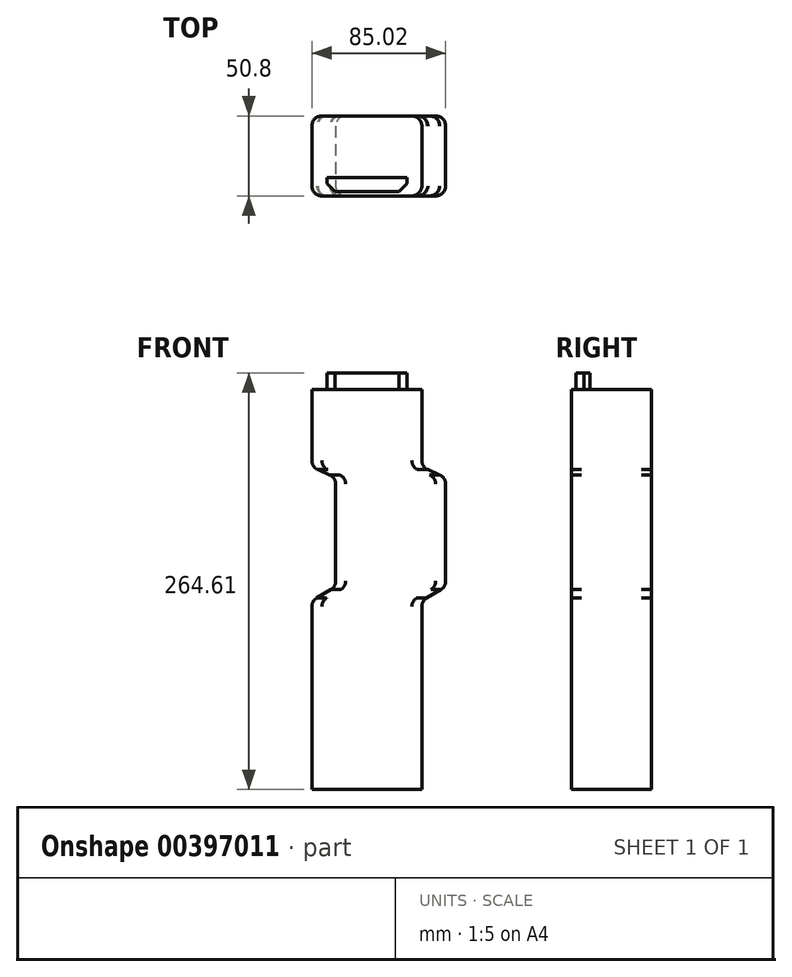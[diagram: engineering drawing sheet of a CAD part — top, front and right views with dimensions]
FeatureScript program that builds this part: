
annotation { "Feature Type Name" : "Feature", "Feature Type Description" : "" }
export const myFeature = defineFeature(function(context is Context, id is Id, definition is map)
    precondition{}
    {
        {
            var Q0;
            Q0=qCreatedBy(makeId("Top.planeOp"),FACE);
            var sketch = newSketch(context, id + "F0", { "sketchPlane" : qUnion([Q0])});
            skLineSegment(sketch, "E0.bottom", {"start": v(-28.57, 25.4) * mm, "end": v(28.57, 25.4) * mm});
            skLineSegment(sketch, "E0.top", {"start": v(-28.57, -25.4) * mm, "end": v(28.58, -25.4) * mm});
            skLineSegment(sketch, "E0.left", {"start": v(-34.92, 19.05) * mm, "end": v(-34.92, -19.05) * mm});
            skLineSegment(sketch, "E0.right", {"start": v(34.93, 19.05) * mm, "end": v(34.93, -19.05) * mm});
            skLineSegment(sketch, "E1", {"start": v(0, 25.4) * mm, "end": v(0, -25.4) * mm, "construction": true});
            skLineSegment(sketch, "E2", {"start": v(-34.92, 0) * mm, "end": v(34.93, 0) * mm, "construction": true});
            skPoint(sketch, "E2.endSnap0", {"position": v(34.93, 0) * mm});
            skPoint(sketch, "E3.visualSharp", {"position": v(-34.92, 25.4) * mm});
            skArc(sketch, "E3.filletArc", {"start": v(-28.57, 25.4) * mm, "mid": v(-33.07, 23.54) * mm, "end": v(-34.93, 19.05) * mm});
            skPoint(sketch, "E4.visualSharp", {"position": v(-34.92, -25.4) * mm});
            skArc(sketch, "E4.filletArc", {"start": v(-34.93, -19.05) * mm, "mid": v(-33.07, -23.54) * mm, "end": v(-28.57, -25.4) * mm});
            skPoint(sketch, "E5.visualSharp", {"position": v(34.93, -25.4) * mm});
            skArc(sketch, "E5.filletArc", {"start": v(28.58, -25.4) * mm, "mid": v(33.07, -23.54) * mm, "end": v(34.93, -19.05) * mm});
            skPoint(sketch, "E6.visualSharp", {"position": v(34.93, 25.4) * mm});
            skArc(sketch, "E6.filletArc", {"start": v(34.93, 19.05) * mm, "mid": v(33.07, 23.54) * mm, "end": v(28.57, 25.4) * mm});
            skSolve(sketch);
        }
        {
            var Q0;
            Q0=qCreatedBy(makeId("Front.planeOp"),FACE);
            var sketch = newSketch(context, id + "F1", { "sketchPlane" : qUnion([Q0])});
            skLineSegment(sketch, "E7", {"start": v(0, 0) * mm, "end": v(0, 116.26) * mm});
            skLineSegment(sketch, "E8", {"start": v(3.12, 121.72) * mm, "end": v(12.04, 127) * mm});
            skLineSegment(sketch, "E9", {"start": v(15.16, 132.47) * mm, "end": v(15.16, 194.1) * mm});
            skLineSegment(sketch, "E10", {"start": v(11.34, 199.93) * mm, "end": v(3.82, 203.2) * mm});
            skLineSegment(sketch, "E11", {"start": v(0, 209.02) * mm, "end": v(0, 254) * mm});
            skPoint(sketch, "E12.visualSharp", {"position": v(0, 204.86) * mm});
            skArc(sketch, "E12.filletArc", {"start": v(0, 209.02) * mm, "mid": v(1.04, 205.54) * mm, "end": v(3.82, 203.2) * mm});
            skPoint(sketch, "E13.visualSharp", {"position": v(15.16, 198.27) * mm});
            skArc(sketch, "E13.filletArc", {"start": v(15.16, 194.1) * mm, "mid": v(14.12, 197.59) * mm, "end": v(11.34, 199.93) * mm});
            skPoint(sketch, "E14.visualSharp", {"position": v(15.16, 128.84) * mm});
            skArc(sketch, "E14.filletArc", {"start": v(12.04, 127) * mm, "mid": v(14.33, 129.32) * mm, "end": v(15.16, 132.47) * mm});
            skPoint(sketch, "E15.visualSharp", {"position": v(0, 119.88) * mm});
            skArc(sketch, "E15.filletArc", {"start": v(3.12, 121.72) * mm, "mid": v(0.83, 119.4) * mm, "end": v(0, 116.26) * mm});
            skSolve(sketch);
        }
        {
            var Q0;
            Q0=makeQuery(id+"F0.imprint","IMPRINT",FACE,{"disambiguationData":[TD([[makeQuery(id+"F0.imprint","IMPRINT",EDGE,{"derivedFrom":sQuery(id+"F0.wireOp",EDGE,"E0.bottom")}),-1.0]])]});
            var Q1;
            Q1 = qConstructionFilter(qBodyType(qCreatedBy(id + "F1" ,EDGE), BodyType.WIRE), ConstructionObject.NO);
            sweep(context, id + "F2", {"profiles" : qUnion([Q0]), "path" : qUnion([Q1]), "keepProfileOrientation" : true});
        }
        {
            var Q0;
            Q0=qCreatedBy(makeId("Right.planeOp"),FACE);
            var sketch = newSketch(context, id + "F3", { "sketchPlane" : qUnion([Q0])});
            skLineSegment(sketch, "E16.bottom", {"start": v(-22.52, 254) * mm, "end": v(-13.82, 254) * mm});
            skLineSegment(sketch, "E16.top", {"start": v(-22.52, 264.6) * mm, "end": v(-13.82, 264.6) * mm});
            skLineSegment(sketch, "E16.left", {"start": v(-22.52, 254) * mm, "end": v(-22.52, 264.6) * mm});
            skLineSegment(sketch, "E16.right", {"start": v(-13.82, 254) * mm, "end": v(-13.82, 264.6) * mm});
            skSolve(sketch);
        }
        {
            var Q0;
            Q0 = qSketchRegion(id + "F3", true);
            extrude(context, id + "F4", {"entities" : qUnion([Q0]), "operationType" : NewBodyOperationType.ADD, "endBound" : BoundingType.SYMMETRIC, "depth" : 50.8 * mm});
        }
        {
            var Q0;
            Q0=makeQuery(id+"F4.opExtrude","CAP_EDGE",EDGE,{"disambiguationData":[OSD([sQuery(id+"F3.wireOp",EDGE,"E16.left")])],"isStart":true});
            var Q1;
            Q1=makeQuery(id+"F4.opExtrude","CAP_EDGE",EDGE,{"disambiguationData":[OSD([sQuery(id+"F3.wireOp",EDGE,"E16.left")])],"isStart":false});
            var Q2;
            Q2=makeQuery(id+"FbDHRJDbNVzI603_1.1.F4.opExtrude","CAP_EDGE",EDGE,{"disambiguationData":[OSD([sQuery(id+"F3.wireOp",EDGE,"E16.left")])],"isStart":false});
            var Q3;
            Q3=makeQuery(id+"FbDHRJDbNVzI603_1.1.F4.opExtrude","CAP_EDGE",EDGE,{"disambiguationData":[OSD([sQuery(id+"F3.wireOp",EDGE,"E16.left")])],"isStart":true});
            chamfer(context, id + "F5", {"entities" : qUnion([Q0, Q1, Q2, Q3]), "width" : 5.08 * mm, "tangentPropagation" : true});
        }
    });
